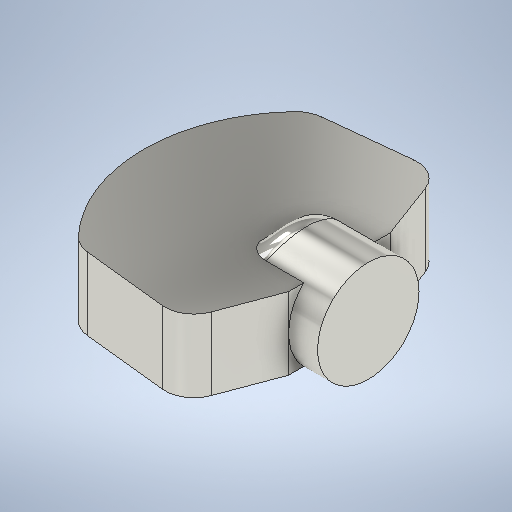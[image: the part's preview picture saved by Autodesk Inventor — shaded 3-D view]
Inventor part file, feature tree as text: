
AUTODESK INVENTOR PART (.ipt)
format: ipt  version: 2025.2 (Build 292293000, 293)  size: 305,664 bytes
history: native  units: in
note: dims shown in document units (in); Inventor stores cm internally (conversion verified against a paired STEP export)
features: extrude x2, fillet x2, sketch x2
ambient origin geometry x8: Origin, YZ Plane, XZ Plane, XY Plane, X Axis, Y Axis, Z Axis, Center Point
bodies: Solid1 (feature_tree)
feature tree (6):
  extrude  "Extrusion1"  Depth=0.1378in
  fillet  "Fillet1"  Radius=0.2106in
  extrude  "Extrusion2"  Depth=0.2106in
  fillet  "Fillet2"  Radius=0.0787in
  sketch  "Sketch1"  dims[d0=0.2756in d1=0.1378in d2=0.2106in]
  sketch  "Sketch2"  dims[d3=0.0787in d4=0.2106in d5=0.0787in d6=0.315in d7=0.315in d8=0.1772in d9=0.1772in d10=0.5315in d11=0.1969in d12=0.0in d13=0.0787in d14=0.2756in d15=0.0in d16=0.0984in d17=0.0787in d18=0.0in d19=0.1575in d20=0.0in d21=0.0787in]
